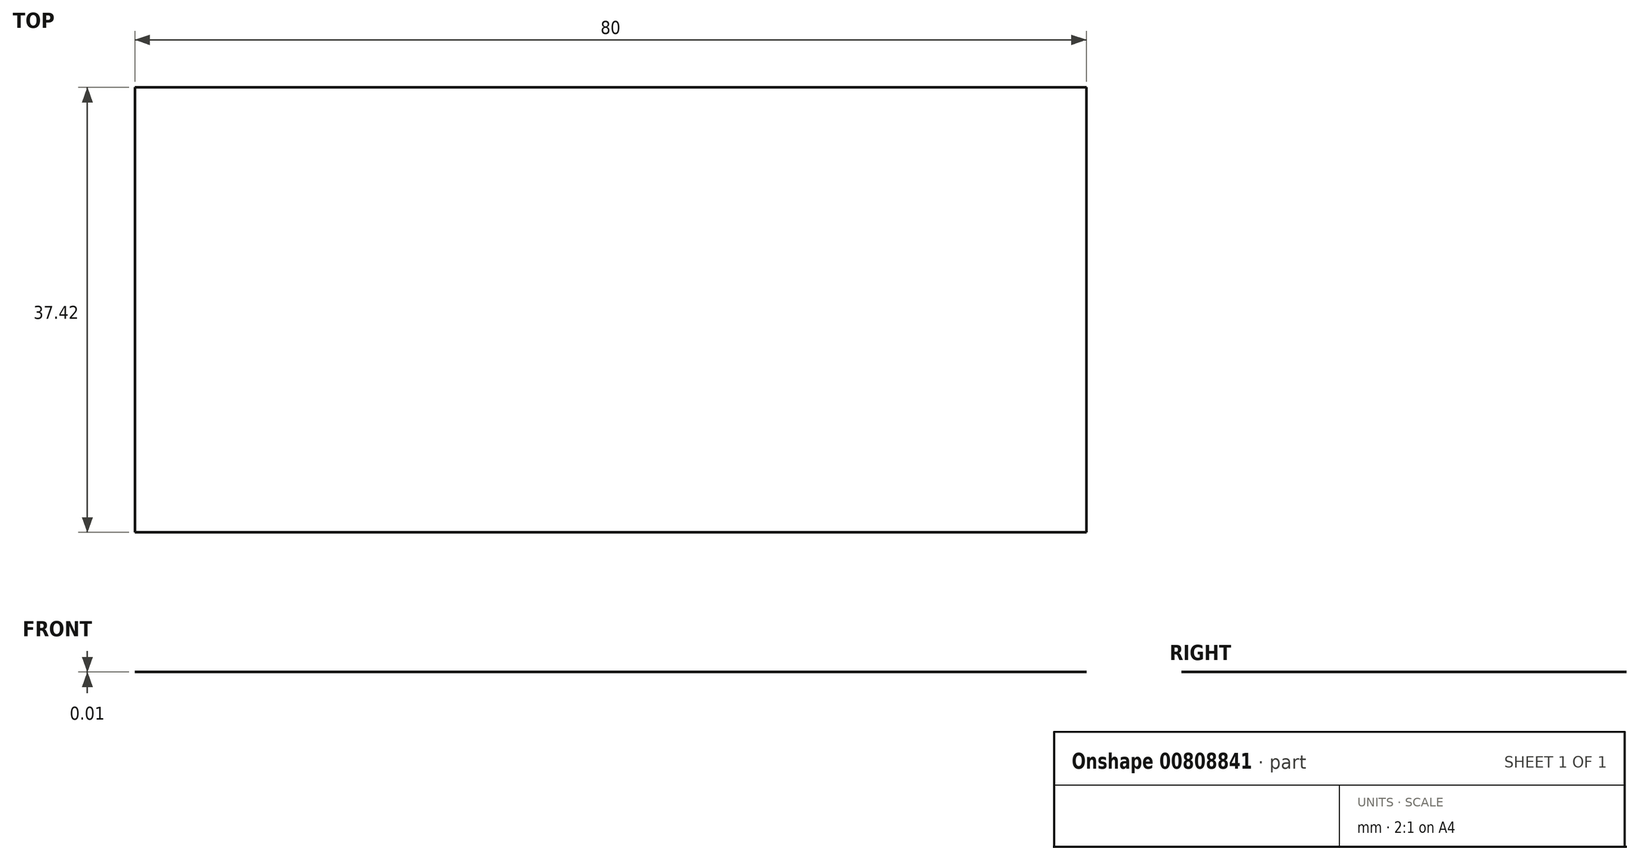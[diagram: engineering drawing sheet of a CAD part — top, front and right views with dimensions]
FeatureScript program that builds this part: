
annotation { "Feature Type Name" : "Feature", "Feature Type Description" : "" }
export const myFeature = defineFeature(function(context is Context, id is Id, definition is map)
    precondition{}
    {
        {
            var Q0;
            Q0=qCreatedBy(makeId("Top.planeOp"),FACE);
            var sketch = newSketch(context, id + "F0", { "sketchPlane" : qUnion([Q0])});
            skLineSegment(sketch, "E0.bottom", {"start": v(-40, 18.7) * mm, "end": v(40, 18.7) * mm});
            skLineSegment(sketch, "E0.top", {"start": v(-40, -18.7) * mm, "end": v(40, -18.7) * mm});
            skLineSegment(sketch, "E0.left", {"start": v(-40, 18.7) * mm, "end": v(-40, -18.7) * mm});
            skLineSegment(sketch, "E0.right", {"start": v(40, 18.7) * mm, "end": v(40, -18.7) * mm});
            skPoint(sketch, "E0.middle", {"position": v(0, 0) * mm});
            skSolve(sketch);
        }
        {
            var Q0;
            Q0=makeQuery(id+"F0.imprint","IMPRINT",FACE,{"disambiguationData":[TD([[makeQuery(id+"F0.imprint","IMPRINT",EDGE,{"derivedFrom":sQuery(id+"F0.wireOp",EDGE,"E0.bottom")}),-1.0]])]});
            extrude(context, id + "F1", {"entities" : qUnion([Q0]), "depth" : 0.01 * mm, "offsetDistance" : 25 * mm});
        }
    });
